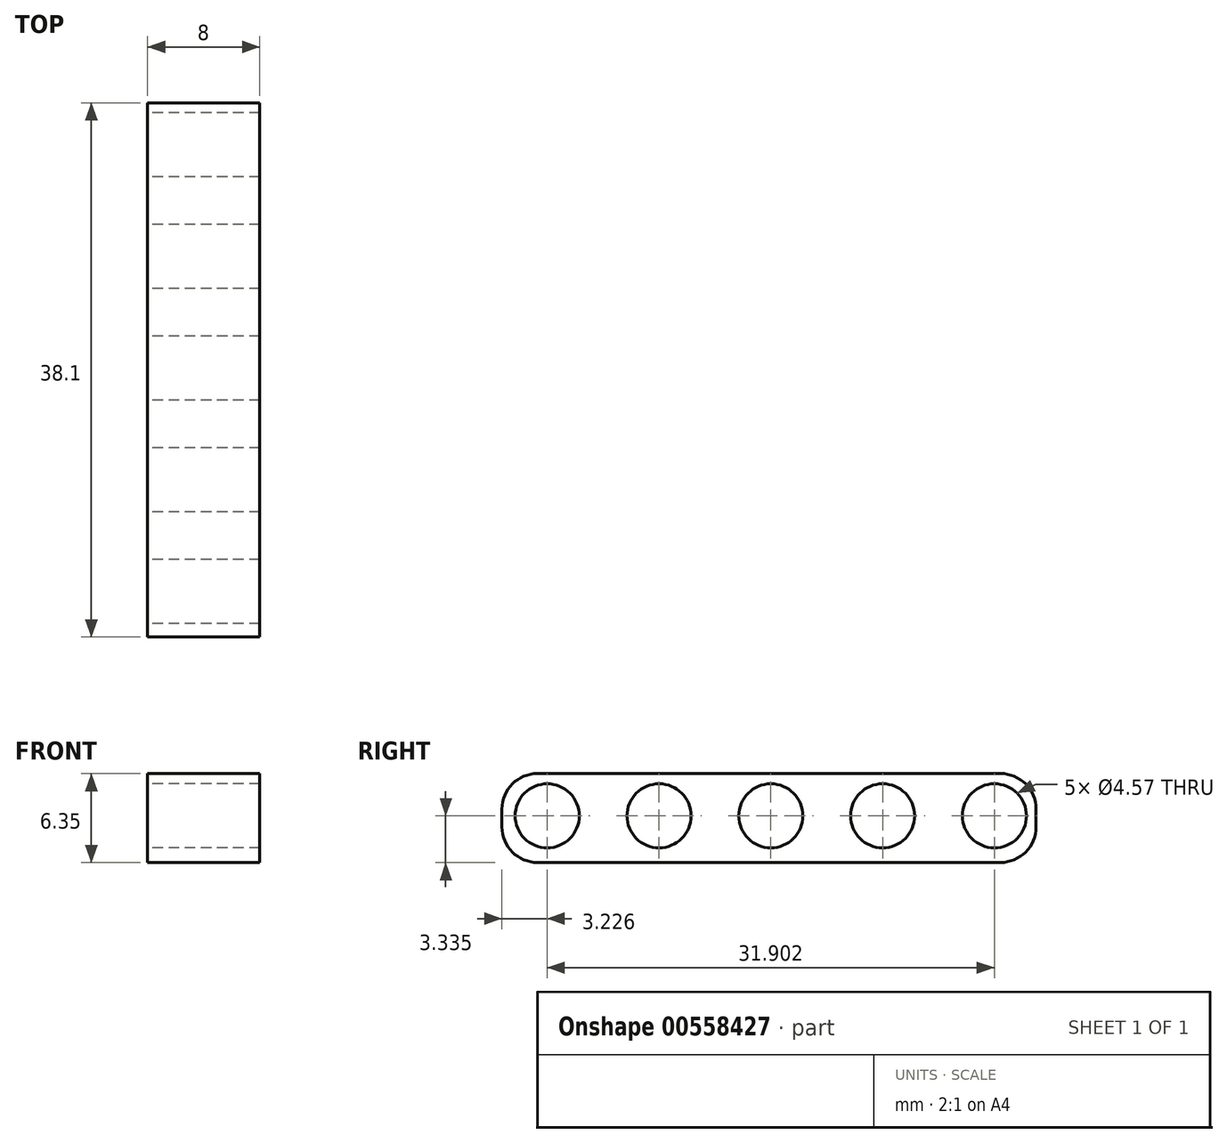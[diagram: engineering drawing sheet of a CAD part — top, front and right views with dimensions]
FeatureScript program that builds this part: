
annotation { "Feature Type Name" : "Feature", "Feature Type Description" : "" }
export const myFeature = defineFeature(function(context is Context, id is Id, definition is map)
    precondition{}
    {
        {
            var Q0;
            Q0=qCreatedBy(makeId("Right.planeOp"),FACE);
            var sketch = newSketch(context, id + "F0", { "sketchPlane" : qUnion([Q0])});
            skLineSegment(sketch, "E0.bottom", {"start": v(-17.17, 2.16) * mm, "end": v(20.93, 2.16) * mm});
            skLineSegment(sketch, "E0.top", {"start": v(-17.17, -4.19) * mm, "end": v(20.93, -4.19) * mm});
            skLineSegment(sketch, "E0.left", {"start": v(-17.17, 2.16) * mm, "end": v(-17.17, -4.19) * mm});
            skLineSegment(sketch, "E0.right", {"start": v(20.93, 2.16) * mm, "end": v(20.93, -4.19) * mm});
            skSolve(sketch);
        }
        {
            var Q0;
            Q0=makeQuery(id+"F0.imprint","IMPRINT",FACE,{"disambiguationData":[TD([[makeQuery(id+"F0.imprint","IMPRINT",EDGE,{"derivedFrom":sQuery(id+"F0.wireOp",EDGE,"E0.bottom")}),-1.0]])]});
            var sketch = newSketch(context, id + "F1", { "sketchPlane" : qUnion([Q0])});
            skCircle(sketch, "E1", {"center": v(-13.94, -0.85) * mm, "radius": 2.29 * mm});
            skCircle(sketch, "E2.1.0.0", {"center": v(-5.97, -0.85) * mm, "radius": 2.29 * mm});
            skCircle(sketch, "E2.2.0.0", {"center": v(2, -0.85) * mm, "radius": 2.29 * mm});
            skCircle(sketch, "E2.3.0.0", {"center": v(9.98, -0.85) * mm, "radius": 2.29 * mm});
            skCircle(sketch, "E2.4.0.0", {"center": v(17.96, -0.85) * mm, "radius": 2.29 * mm});
            skLineSegment(sketch, "E2.direction1", {"start": v(-13.94, -0.85) * mm, "end": v(-5.97, -0.85) * mm, "construction": true});
            skSolve(sketch);
        }
        {
            var Q0;
            Q0=makeQuery(id+"F0.imprint","IMPRINT",FACE,{"disambiguationData":[TD([[makeQuery(id+"F0.imprint","IMPRINT",EDGE,{"derivedFrom":sQuery(id+"F0.wireOp",EDGE,"E0.bottom")}),-1.0]])]});
            extrude(context, id + "F2", {"entities" : qUnion([Q0]), "depth" : 8 * mm, "offsetDistance" : 25.4 * mm});
        }
        {
            var Q0;
            Q0 = qSketchRegion(id + "F1", true);
            extrude(context, id + "F3", {"entities" : qUnion([Q0]), "operationType" : NewBodyOperationType.REMOVE, "depth" : 25.4 * mm, "offsetDistance" : 25.4 * mm});
        }
        {
            var Q0;
            Q0=makeQuery(id+"F2.opExtrude","SWEPT_EDGE",EDGE,{"disambiguationData":[OSD([sQuery(id+"F0.wireOp",EDGE,"E0.bottom"),sQuery(id+"F0.wireOp",EDGE,"E0.left")])]});
            fillet(context, id + "F4", {"entities" : qUnion([Q0]), "radius" : 2.54 * mm, "tangentPropagation" : true, "allowEdgeOverflow" : false});
        }
        {
            var Q0;
            Q0=makeQuery(id+"F2.opExtrude","SWEPT_EDGE",EDGE,{"disambiguationData":[OSD([sQuery(id+"F0.wireOp",EDGE,"E0.top"),sQuery(id+"F0.wireOp",EDGE,"E0.left")])]});
            fillet(context, id + "F5", {"entities" : qUnion([Q0]), "radius" : 2.54 * mm, "tangentPropagation" : true, "allowEdgeOverflow" : false});
        }
        {
            var Q0;
            Q0=makeQuery(id+"F2.opExtrude","SWEPT_EDGE",EDGE,{"disambiguationData":[OSD([sQuery(id+"F0.wireOp",EDGE,"E0.bottom"),sQuery(id+"F0.wireOp",EDGE,"E0.right")])]});
            fillet(context, id + "F6", {"entities" : qUnion([Q0]), "radius" : 2.54 * mm, "tangentPropagation" : true, "allowEdgeOverflow" : false});
        }
        {
            var Q0;
            Q0=makeQuery(id+"F2.opExtrude","SWEPT_EDGE",EDGE,{"disambiguationData":[OSD([sQuery(id+"F0.wireOp",EDGE,"E0.top"),sQuery(id+"F0.wireOp",EDGE,"E0.right")])]});
            fillet(context, id + "F7", {"entities" : qUnion([Q0]), "radius" : 2.54 * mm, "tangentPropagation" : true, "allowEdgeOverflow" : false});
        }
    });
